# Revit family: QF_Kienle_SF
name_source: partatom
category: Sonderausstattung
units: mm (PartAtom-declared; Revit-internal decimal feet)

## family parameters
Arbeitsebenenbasiert = Nein
Beim Laden mit Abzugskörper schneiden = Nein
Bemaßung runder Anschluss = Durchmesser verwenden
Beschriftungsausrichtung beibehalten = Nein
Gemeinsam genutzt = Nein
Immer vertikal = Ja
OmniClass-Nummer = 23.40.40.14.17
OmniClass-Titel = Food Cooking Equipment
Raumberechnungspunkt = Nein
Schneiden in Ansichten zulassen = Nein
Teiletyp = Normal

## types (1)
- 1NAC - 230 V - 50 Hz
    Anzahl der Pole = 1
    Beschreibung = Warmhaltegerät (GN 1/1), Standmodell
    CE Kennzeichnung = Ja
    Frequenz = 50 Hz
    Gewicht = 35.00 kg
    Hersteller = Kienle
    IP Schutzart = 54
    Kosten = 0 $
    Länge Gerätebreite = 403 mm
    Modell = SF
    Phasen = 1
    Sensible Abwärme Belastung = 280 W
    Spannung = 230 V
    Stecker System = CEE 7
    Tiefe = 680 mm
    URL = https://www.kienle-fritteusen.de
    Vorgabe-Ansicht = 0 mm  [stored 0 ft]
    Warnhinweise = W017 / W012 (ISO 7010)
    Watt Leistung = 800 W

note: [stored X ft] marks values corroborated as IEEE doubles in the binary element streams (Revit-internal decimal feet)
